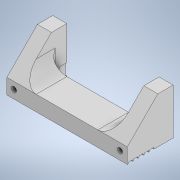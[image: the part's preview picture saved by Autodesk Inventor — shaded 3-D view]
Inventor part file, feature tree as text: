
AUTODESK INVENTOR PART (.ipt)
format: ipt  version: 2021 (Build 250183000, 183)  size: 710,144 bytes
history: native  units: in
note: dims shown in document units (in); Inventor stores cm internally (conversion verified against a paired STEP export)
features: sketch x8, extrude x7, projected_geometry x7, mirror x4, pattern_linear x3, fillet x2, chamfer x2, hole x1
ambient origin geometry x8: Origin, YZ Plane, XZ Plane, XY Plane, X Axis, Y Axis, Z Axis, Center Point
bodies: Solid1 (feature_tree)
feature tree (34):
  extrude  "Extrusion1"  Depth=0.5in
  extrude  "Extrusion2"  Depth=0.5in
  mirror  "Mirror1"
  fillet  "Fillet1"  Radius=0.5in
  extrude  "Extrusion3"  Depth=0.125in
  pattern_linear  "Rectangular Pattern1"  Count1=11 Spacing1=0.25in
  extrude  "Extrusion4"  Depth=0.375in
  mirror  "Mirror2"
  hole  "Hole1"  [1 undecoded]
  mirror  "Mirror3"
  extrude  "Extrusion5"  Depth=0.19in
  chamfer  "Chamfer2"  Distance=0.236in
  fillet  "Fillet3"  Radius=0.8108in
  chamfer  "Chamfer3"  Distance=1.0in
  extrude  "Extrusion9"  Depth=0.125in TaperAngle=45.0deg
  pattern_linear  "Rectangular Pattern5"  Spacing1=0.5in  [1 undecoded]
  extrude  "Extrusion10"  Depth=0.125in TaperAngle=45.0deg
  pattern_linear  "Rectangular Pattern6"  Spacing1=4.1in  [1 undecoded]
  mirror  "Mirror5"
  sketch  "Sketch1"  dims[d0=3.938in d1=0.5in]
  sketch  "Sketch2"  dims[d2=1.0in d3=0.0in d4=0.46in d5=0.5in d6=0.0in]
  projected_geometry  "Projected Loop1"
  sketch  "Sketch3"  dims[d7=0.125in d9=0.162in]
  projected_geometry  "Projected Loop2"
  sketch  "Sketch4"  dims[d10=0.087in]
  projected_geometry  "Projected Loop3"
  projected_geometry  "Projected Loop4"
  sketch  "Sketch5"  dims[d11=0.0625in d12=0.0in d13=4.3307in d15=0.25in]
  projected_geometry  "Projected Loop5"
  projected_geometry  "Projected Loop6"
  sketch  "Sketch6"  dims[d19=0.04in d20=0.375in]
  projected_geometry  "Projected Loop7"
  sketch  "Sketch9"  dims[d21=0.02in d22=0.25in d23=0.0in]
  sketch  "Sketch10"  dims[d24=0.266in d25=0.276in d26=0.236in d27=0.17in d28=0.75in d29=0.507in d30=0.25in d31=0.5635in d32=0.12in d33=0.8108in d34=1.0in d35=0.0in d36=1.0in d37=0.125in d38=45.0deg d39=0.5in d41=0.01in d42=0.125in d43=45.0deg d71=4.1in d72=0.15in d73=0.125in d74=2.05in d75=0.05in d76=-0.1031in d77=1.9685in d79=0.175in d80=0.125in d81=0.51in d82=0.05in d83=0.05in d84=0.0in d85=0.7874in d87=0.19in]
note: 3 required parameter values undecoded (feature->parameter linkage not recoverable at this tier; creation-order binding heuristic only, values carry confidence <= 0.55)
